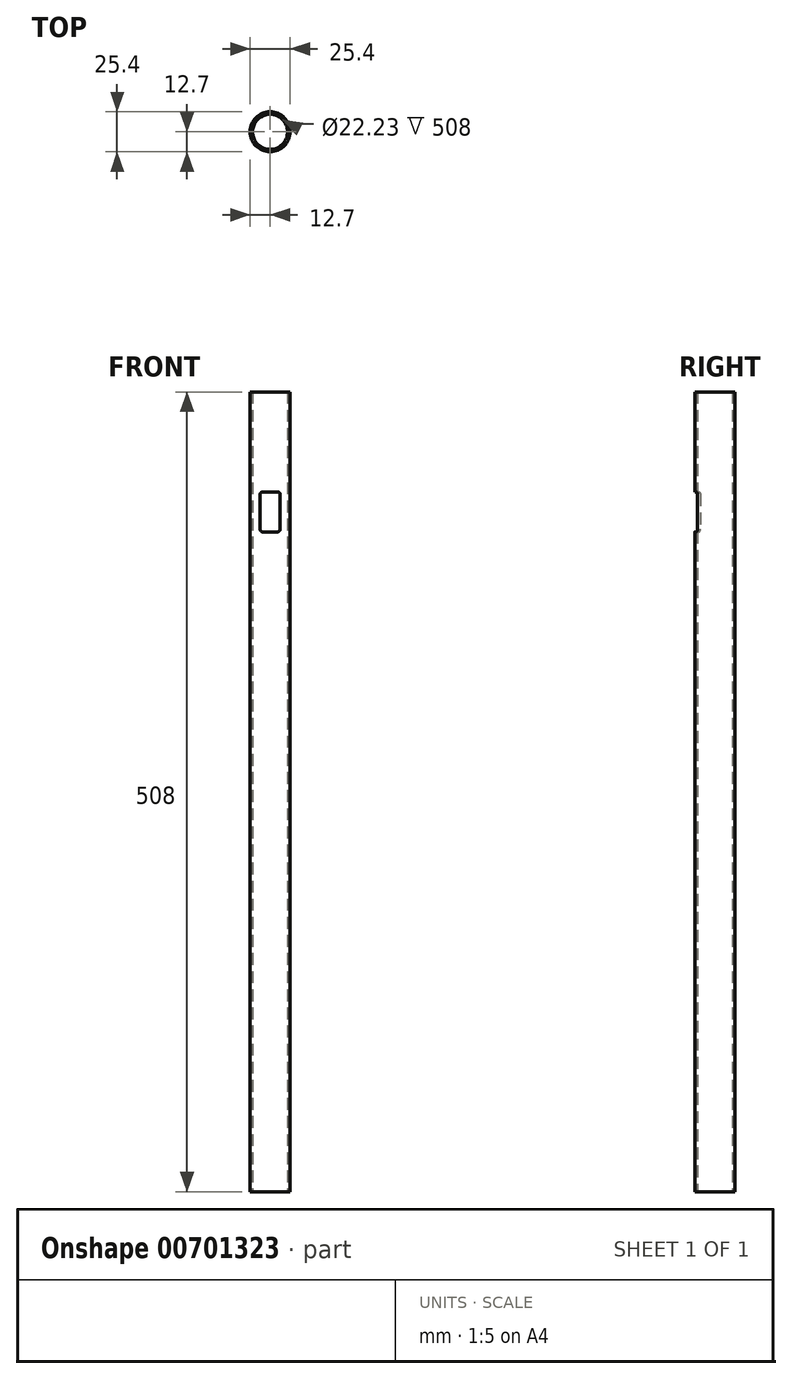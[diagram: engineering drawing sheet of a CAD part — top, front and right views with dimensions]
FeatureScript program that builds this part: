
annotation { "Feature Type Name" : "Feature", "Feature Type Description" : "" }
export const myFeature = defineFeature(function(context is Context, id is Id, definition is map)
    precondition{}
    {
        {
            var Q0;
            Q0=qCreatedBy(makeId("Top.planeOp"),FACE);
            var sketch = newSketch(context, id + "F0", { "sketchPlane" : qUnion([Q0])});
            skCircle(sketch, "E0", {"center": v(0, 0) * mm, "radius": 11.11 * mm});
            skCircle(sketch, "E1", {"center": v(0, 0) * mm, "radius": 12.7 * mm});
            skSolve(sketch);
        }
        {
            var Q0;
            Q0 = qSketchRegion(id + "F0", true);
            extrude(context, id + "F1", {"entities" : qUnion([Q0]), "endBound" : BoundingType.SYMMETRIC, "depth" : 508 * mm, "offsetDistance" : 25.4 * mm});
        }
        {
            var Q0;
            Q0=qCreatedBy(makeId("Front.planeOp"),FACE);
            var sketch = newSketch(context, id + "F2", { "sketchPlane" : qUnion([Q0])});
            skLineSegment(sketch, "E2.bottom", {"start": v(-4.7, 190.5) * mm, "end": v(4.7, 190.5) * mm});
            skLineSegment(sketch, "E2.top", {"start": v(-4.7, 165.1) * mm, "end": v(4.7, 165.1) * mm});
            skLineSegment(sketch, "E2.left", {"start": v(-6.35, 188.85) * mm, "end": v(-6.35, 166.75) * mm});
            skLineSegment(sketch, "E2.right", {"start": v(6.35, 188.85) * mm, "end": v(6.35, 166.75) * mm});
            skPoint(sketch, "E3.visualSharp", {"position": v(-6.35, 190.5) * mm});
            skArc(sketch, "E3.filletArc", {"start": v(-4.7, 190.5) * mm, "mid": v(-5.87, 190.02) * mm, "end": v(-6.35, 188.85) * mm});
            skPoint(sketch, "E4.visualSharp", {"position": v(6.35, 190.5) * mm});
            skArc(sketch, "E4.filletArc", {"start": v(6.35, 188.85) * mm, "mid": v(5.87, 190.02) * mm, "end": v(4.7, 190.5) * mm});
            skPoint(sketch, "E5.visualSharp", {"position": v(6.35, 165.1) * mm});
            skArc(sketch, "E5.filletArc", {"start": v(4.7, 165.1) * mm, "mid": v(5.87, 165.58) * mm, "end": v(6.35, 166.75) * mm});
            skPoint(sketch, "E6.visualSharp", {"position": v(-6.35, 165.1) * mm});
            skArc(sketch, "E6.filletArc", {"start": v(-6.35, 166.75) * mm, "mid": v(-5.87, 165.58) * mm, "end": v(-4.7, 165.1) * mm});
            skLineSegment(sketch, "E7", {"start": v(0, 165.1) * mm, "end": v(0, 11.02) * mm, "construction": true});
            skSolve(sketch);
        }
        {
            var Q0;
            Q0 = qSketchRegion(id + "F2", true);
            extrude(context, id + "F3", {"entities" : qUnion([Q0]), "operationType" : NewBodyOperationType.REMOVE, "depth" : 25.4 * mm, "offsetDistance" : 25.4 * mm});
        }
    });
